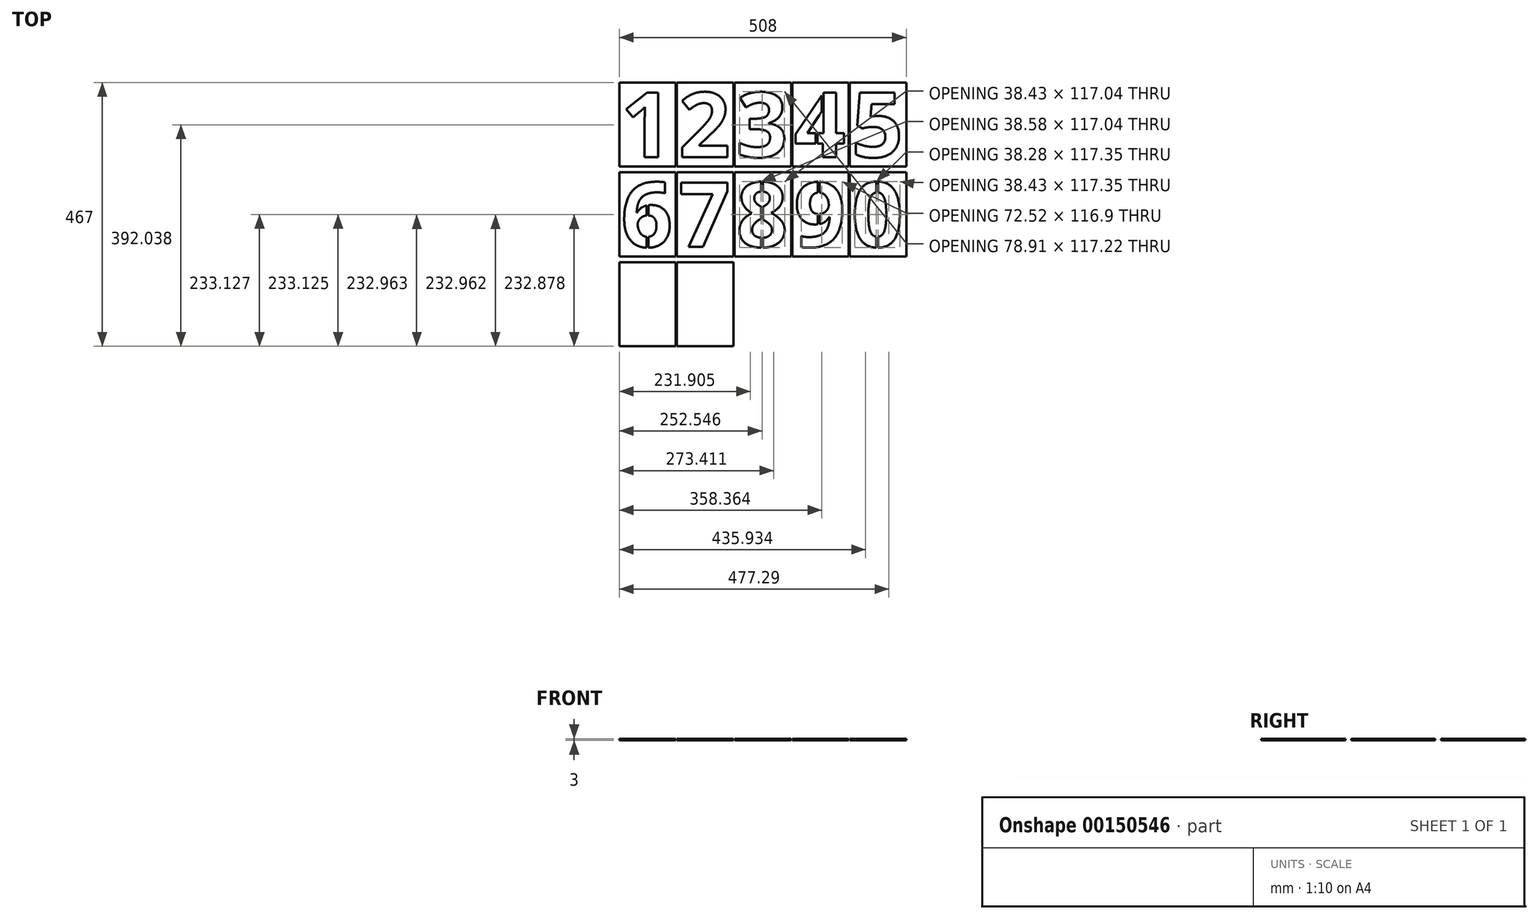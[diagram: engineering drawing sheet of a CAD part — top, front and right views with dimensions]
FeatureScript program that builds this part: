
annotation { "Feature Type Name" : "Feature", "Feature Type Description" : "" }
export const myFeature = defineFeature(function(context is Context, id is Id, definition is map)
    precondition{}
    {
        {
            var Q0;
            Q0=qCreatedBy(makeId("Top.planeOp"),FACE);
            var sketch = newSketch(context, id + "F0", { "sketchPlane" : qUnion([Q0])});
            skLineSegment(sketch, "E0.top", {"start": v(274, 333) * mm, "end": v(-274, 333) * mm, "construction": true});
            skLineSegment(sketch, "E0.left", {"start": v(274, -174) * mm, "end": v(274, 333) * mm, "construction": true});
            skLineSegment(sketch, "E0.right", {"start": v(-274, -174) * mm, "end": v(-274, 333) * mm, "construction": true});
            skPoint(sketch, "E0.middle", {"position": v(0, 0) * mm});
            skLineSegment(sketch, "E1", {"start": v(-254, 333) * mm, "end": v(-254, -174) * mm, "construction": true});
            skLineSegment(sketch, "E2.bottom", {"start": v(-254, 313) * mm, "end": v(274, 313) * mm, "construction": true});
            skLineSegment(sketch, "E2.top", {"start": v(-254, 164) * mm, "end": v(274, 164) * mm, "construction": true});
            skLineSegment(sketch, "E2.left", {"start": v(-254, 313) * mm, "end": v(-254, 164) * mm});
            skLineSegment(sketch, "E3", {"start": v(-154, 313) * mm, "end": v(-154, 164) * mm});
            skLineSegment(sketch, "E4", {"start": v(-254, 313) * mm, "end": v(-154, 313) * mm});
            skLineSegment(sketch, "E5", {"start": v(-254, 164) * mm, "end": v(-154, 164) * mm});
            skLineSegment(sketch, "E6.0", {"start": v(-152, 313) * mm, "end": v(-152, 164) * mm});
            skLineSegment(sketch, "E7", {"start": v(-52, 313) * mm, "end": v(-52, 164) * mm});
            skLineSegment(sketch, "E8.0", {"start": v(-50, 313) * mm, "end": v(-50, 164) * mm});
            skLineSegment(sketch, "E9", {"start": v(-152, 313) * mm, "end": v(-52, 313) * mm});
            skLineSegment(sketch, "E10", {"start": v(-152, 164) * mm, "end": v(-52, 164) * mm});
            skLineSegment(sketch, "E11", {"start": v(50, 313) * mm, "end": v(50, 164) * mm});
            skLineSegment(sketch, "E12.0", {"start": v(52, 313) * mm, "end": v(52, 164) * mm});
            skLineSegment(sketch, "E13", {"start": v(152, 313) * mm, "end": v(152, 164) * mm});
            skLineSegment(sketch, "E14.0", {"start": v(154, 313) * mm, "end": v(154, 164) * mm});
            skLineSegment(sketch, "E15", {"start": v(254, 313) * mm, "end": v(254, 164) * mm});
            skLineSegment(sketch, "E16", {"start": v(-50, 313) * mm, "end": v(50, 313) * mm});
            skLineSegment(sketch, "E17", {"start": v(52, 313) * mm, "end": v(152, 313) * mm});
            skLineSegment(sketch, "E18", {"start": v(154, 313) * mm, "end": v(254, 313) * mm});
            skLineSegment(sketch, "E19", {"start": v(254, 164) * mm, "end": v(154, 164) * mm});
            skLineSegment(sketch, "E20", {"start": v(152, 164) * mm, "end": v(52, 164) * mm});
            skLineSegment(sketch, "E21", {"start": v(50, 164) * mm, "end": v(-50, 164) * mm});
            skLineSegment(sketch, "E22.0", {"start": v(-261, 159) * mm, "end": v(267, 159) * mm, "construction": true});
            skLineSegment(sketch, "E23.MirrorCS", {"start": v(-52, 5) * mm, "end": v(-52, 154) * mm});
            skLineSegment(sketch, "E24.MirrorCS", {"start": v(254, 5) * mm, "end": v(254, 154) * mm});
            skLineSegment(sketch, "E25.MirrorCS", {"start": v(-254, 154) * mm, "end": v(-154, 154) * mm});
            skLineSegment(sketch, "E26.MirrorCS", {"start": v(-254, 5) * mm, "end": v(-154, 5) * mm});
            skLineSegment(sketch, "E27.MirrorCS", {"start": v(-152, 154) * mm, "end": v(-52, 154) * mm});
            skLineSegment(sketch, "E28.MirrorCS", {"start": v(154, 5) * mm, "end": v(254, 5) * mm});
            skLineSegment(sketch, "E29.MirrorCS", {"start": v(-152, 5) * mm, "end": v(-152, 154) * mm});
            skLineSegment(sketch, "E30.MirrorCS", {"start": v(154, 5) * mm, "end": v(154, 154) * mm});
            skLineSegment(sketch, "E31.MirrorCS", {"start": v(52, 5) * mm, "end": v(52, 154) * mm});
            skLineSegment(sketch, "E32.MirrorCS", {"start": v(-50, 5) * mm, "end": v(50, 5) * mm});
            skLineSegment(sketch, "E33.MirrorCS", {"start": v(-152, 5) * mm, "end": v(-52, 5) * mm});
            skLineSegment(sketch, "E34.MirrorCS", {"start": v(52, 5) * mm, "end": v(152, 5) * mm});
            skLineSegment(sketch, "E35.MirrorCS", {"start": v(50, 5) * mm, "end": v(50, 154) * mm});
            skLineSegment(sketch, "E36.MirrorCS", {"start": v(254, 154) * mm, "end": v(154, 154) * mm});
            skLineSegment(sketch, "E37.MirrorCS", {"start": v(-254, 5) * mm, "end": v(-254, 154) * mm});
            skLineSegment(sketch, "E38.MirrorCS", {"start": v(-154, 5) * mm, "end": v(-154, 154) * mm});
            skLineSegment(sketch, "E39.MirrorCS", {"start": v(50, 154) * mm, "end": v(-50, 154) * mm});
            skLineSegment(sketch, "E40.MirrorCS", {"start": v(152, 5) * mm, "end": v(152, 154) * mm});
            skLineSegment(sketch, "E41.MirrorCS", {"start": v(152, 154) * mm, "end": v(52, 154) * mm});
            skLineSegment(sketch, "E42.MirrorCS", {"start": v(-50, 5) * mm, "end": v(-50, 154) * mm});
            skLineSegment(sketch, "E43", {"start": v(-254, 0) * mm, "end": v(274, 0) * mm, "construction": true});
            skLineSegment(sketch, "E44.MirrorCS", {"start": v(-152, -5) * mm, "end": v(-152, -154) * mm});
            skLineSegment(sketch, "E45.MirrorCS", {"start": v(-152, -154) * mm, "end": v(-52, -154) * mm});
            skLineSegment(sketch, "E46.MirrorCS", {"start": v(-254, -5) * mm, "end": v(-154, -5) * mm});
            skLineSegment(sketch, "E47.MirrorCS", {"start": v(-254, -154) * mm, "end": v(-154, -154) * mm});
            skLineSegment(sketch, "E48.MirrorCS", {"start": v(-52, -5) * mm, "end": v(-52, -154) * mm});
            skLineSegment(sketch, "E49.MirrorCS", {"start": v(-152, -5) * mm, "end": v(-52, -5) * mm});
            skLineSegment(sketch, "E50.MirrorCS", {"start": v(-154, -5) * mm, "end": v(-154, -154) * mm});
            skLineSegment(sketch, "E51.MirrorCS", {"start": v(-254, -5) * mm, "end": v(-254, -154) * mm});
            skLineSegment(sketch, "E52", {"start": v(-254, 181) * mm, "end": v(254, 181) * mm, "construction": true});
            skLineSegment(sketch, "E53", {"start": v(-251, 313) * mm, "end": v(-251, 159) * mm, "construction": true});
            skText(sketch, "E54", { "text": "1", "fontName": "OpenSans-Bold.ttf"});
            skLineSegment(sketch, "E55", {"start": v(-149, 313) * mm, "end": v(-149, -154) * mm, "construction": true});
            skText(sketch, "E56", { "text": "2", "fontName": "OpenSans-Bold.ttf"});
            skLineSegment(sketch, "E57", {"start": v(-47, 313) * mm, "end": v(-47, 5) * mm, "construction": true});
            skText(sketch, "E58", { "text": "3", "fontName": "OpenSans-Bold.ttf"});
            skLineSegment(sketch, "E59", {"start": v(55, 313) * mm, "end": v(55, 5) * mm, "construction": true});
            skText(sketch, "E60", { "text": "4", "fontName": "OpenSans-Bold.ttf"});
            skLineSegment(sketch, "E61", {"start": v(157.03, 313) * mm, "end": v(157.03, 5) * mm, "construction": true});
            skText(sketch, "E62", { "text": "5", "fontName": "OpenSans-Bold.ttf"});
            skLineSegment(sketch, "E63", {"start": v(-254, 22) * mm, "end": v(254, 22) * mm, "construction": true});
            skLineSegment(sketch, "E64", {"start": v(-251, 159) * mm, "end": v(-251, 0) * mm, "construction": true});
            skText(sketch, "E65", { "text": "6", "fontName": "OpenSans-Bold.ttf"});
            skText(sketch, "E66", { "text": "7", "fontName": "OpenSans-Bold.ttf"});
            skText(sketch, "E67", { "text": "8\n", "fontName": "OpenSans-Bold.ttf"});
            skText(sketch, "E68", { "text": "9", "fontName": "OpenSans-Bold.ttf"});
            skText(sketch, "E69", { "text": "0", "fontName": "OpenSans-Bold.ttf"});
            skLineSegment(sketch, "E70", {"start": v(-274, -174) * mm, "end": v(274, -174) * mm, "construction": true});
            const initialGuessF0  = {"E54": [-0.251, 0.181, 1, 0, 0.115], "E56": [-0.149, 0.181, 1, 0, 0.115], "E58": [-0.047, 0.181, 1, 0, 0.115], "E60": [0.055, 0.181, 1, 0, 0.115], "E62": [0.15703, 0.181, 1, 0, 0.115], "E65": [-0.251, 0.022, 1, 0, 0.115], "E66": [-0.149, 0.022, 1, 0, 0.115], "E67": [-0.047, 0.022, 1, 0, 0.115], "E68": [0.055, 0.022, 1, 0, 0.115], "E69": [0.15703, 0.022, 1, 0, 0.115]};
            skSetInitialGuess(sketch, initialGuessF0);
            skSolve(sketch);
        }
        {
            var Q0;
            Q0=makeQuery(id+"F0.imprint","IMPRINT",FACE,{"disambiguationData":[TD([[makeQuery(id+"F0.imprint","IMPRINT",EDGE,{"derivedFrom":sQuery(id+"F0.wireOp",EDGE,"E2.left")}),1.0]])]});
            var Q1;
            Q1=makeQuery(id+"F0.imprint","IMPRINT",FACE,{"disambiguationData":[TD([[makeQuery(id+"F0.imprint","IMPRINT",EDGE,{"derivedFrom":sQuery(id+"F0.wireOp",EDGE,"E6.0")}),1.0]])]});
            var Q2;
            Q2=makeQuery(id+"F0.imprint","IMPRINT",FACE,{"disambiguationData":[TD([[makeQuery(id+"F0.imprint","IMPRINT",EDGE,{"derivedFrom":sQuery(id+"F0.wireOp",EDGE,"E8.0")}),1.0]])]});
            var Q3;
            Q3=makeQuery(id+"F0.imprint","IMPRINT",FACE,{"disambiguationData":[TD([[makeQuery(id+"F0.imprint","IMPRINT",EDGE,{"derivedFrom":sQuery(id+"F0.wireOp",EDGE,"E12.0")}),1.0]])]});
            var Q4;
            Q4=makeQuery(id+"F0.imprint","IMPRINT",FACE,{"disambiguationData":[TD([[makeQuery(id+"F0.imprint","IMPRINT",EDGE,{"derivedFrom":sQuery(id+"F0.wireOp",EDGE,"E60.sketch_text.stroke-11")}),1.0]])]});
            var Q5;
            Q5=makeQuery(id+"F0.imprint","IMPRINT",FACE,{"disambiguationData":[TD([[makeQuery(id+"F0.imprint","IMPRINT",EDGE,{"derivedFrom":sQuery(id+"F0.wireOp",EDGE,"E14.0")}),1.0]])]});
            var Q6;
            Q6=makeQuery(id+"F0.imprint","IMPRINT",FACE,{"disambiguationData":[TD([[makeQuery(id+"F0.imprint","IMPRINT",EDGE,{"derivedFrom":sQuery(id+"F0.wireOp",EDGE,"E25.MirrorCS")}),-1.0]])]});
            var Q7;
            Q7=makeQuery(id+"F0.imprint","IMPRINT",FACE,{"disambiguationData":[TD([[makeQuery(id+"F0.imprint","IMPRINT",EDGE,{"derivedFrom":sQuery(id+"F0.wireOp",EDGE,"E65.sketch_text.stroke-17")}),1.0]])]});
            var Q8;
            Q8=makeQuery(id+"F0.imprint","IMPRINT",FACE,{"disambiguationData":[TD([[makeQuery(id+"F0.imprint","IMPRINT",EDGE,{"derivedFrom":sQuery(id+"F0.wireOp",EDGE,"E23.MirrorCS")}),1.0]])]});
            var Q9;
            Q9=makeQuery(id+"F0.imprint","IMPRINT",FACE,{"disambiguationData":[TD([[makeQuery(id+"F0.imprint","IMPRINT",EDGE,{"derivedFrom":sQuery(id+"F0.wireOp",EDGE,"E32.MirrorCS")}),1.0]])]});
            var Q10;
            Q10=makeQuery(id+"F0.imprint","IMPRINT",FACE,{"disambiguationData":[TD([[makeQuery(id+"F0.imprint","IMPRINT",EDGE,{"derivedFrom":sQuery(id+"F0.wireOp",EDGE,"E67.sketch_text.stroke-23")}),1.0]])]});
            var Q11;
            Q11=makeQuery(id+"F0.imprint","IMPRINT",FACE,{"disambiguationData":[TD([[makeQuery(id+"F0.imprint","IMPRINT",EDGE,{"derivedFrom":sQuery(id+"F0.wireOp",EDGE,"E67.sketch_text.stroke-16")}),1.0]])]});
            var Q12;
            Q12=makeQuery(id+"F0.imprint","IMPRINT",FACE,{"disambiguationData":[TD([[makeQuery(id+"F0.imprint","IMPRINT",EDGE,{"derivedFrom":sQuery(id+"F0.wireOp",EDGE,"E68.sketch_text.stroke-18")}),1.0]])]});
            var Q13;
            Q13=makeQuery(id+"F0.imprint","IMPRINT",FACE,{"disambiguationData":[TD([[makeQuery(id+"F0.imprint","IMPRINT",EDGE,{"derivedFrom":sQuery(id+"F0.wireOp",EDGE,"E31.MirrorCS")}),-1.0]])]});
            var Q14;
            Q14=makeQuery(id+"F0.imprint","IMPRINT",FACE,{"disambiguationData":[TD([[makeQuery(id+"F0.imprint","IMPRINT",EDGE,{"derivedFrom":sQuery(id+"F0.wireOp",EDGE,"E69.sketch_text.stroke-8")}),1.0]])]});
            var Q15;
            Q15=makeQuery(id+"F0.imprint","IMPRINT",FACE,{"disambiguationData":[TD([[makeQuery(id+"F0.imprint","IMPRINT",EDGE,{"derivedFrom":sQuery(id+"F0.wireOp",EDGE,"E24.MirrorCS")}),1.0]])]});
            var Q16;
            Q16=makeQuery(id+"F0.imprint","IMPRINT",FACE,{"disambiguationData":[TD([[makeQuery(id+"F0.imprint","IMPRINT",EDGE,{"derivedFrom":sQuery(id+"F0.wireOp",EDGE,"E46.MirrorCS")}),-1.0]])]});
            var Q17;
            Q17=makeQuery(id+"F0.imprint","IMPRINT",FACE,{"disambiguationData":[TD([[makeQuery(id+"F0.imprint","IMPRINT",EDGE,{"derivedFrom":sQuery(id+"F0.wireOp",EDGE,"E44.MirrorCS")}),1.0]])]});
            extrude(context, id + "F1", {"entities" : qUnion([Q0, Q1, Q2, Q3, Q4, Q5, Q6, Q7, Q8, Q9, Q10, Q11, Q12, Q13, Q14, Q15, Q16, Q17]), "depth" : 3 * mm});
        }
        {
            var Q0;
            Q0=makeQuery(id+"F1.opExtrude","CAP_FACE",FACE,{"disambiguationData":[OSD([sQuery(id+"F0.wireOp",EDGE,"E12.0"),sQuery(id+"F0.wireOp",EDGE,"E13"),sQuery(id+"F0.wireOp",EDGE,"E17"),sQuery(id+"F0.wireOp",EDGE,"E20"),sQuery(id+"F0.wireOp",EDGE,"E60.sketch_text.stroke-0"),sQuery(id+"F0.wireOp",EDGE,"E60.sketch_text.stroke-1"),sQuery(id+"F0.wireOp",EDGE,"E60.sketch_text.stroke-2"),sQuery(id+"F0.wireOp",EDGE,"E60.sketch_text.stroke-3"),sQuery(id+"F0.wireOp",EDGE,"E60.sketch_text.stroke-4"),sQuery(id+"F0.wireOp",EDGE,"E60.sketch_text.stroke-5"),sQuery(id+"F0.wireOp",EDGE,"E60.sketch_text.stroke-6"),sQuery(id+"F0.wireOp",EDGE,"E60.sketch_text.stroke-7"),sQuery(id+"F0.wireOp",EDGE,"E60.sketch_text.stroke-8"),sQuery(id+"F0.wireOp",EDGE,"E60.sketch_text.stroke-9"),sQuery(id+"F0.wireOp",EDGE,"E60.sketch_text.stroke-10")])],"isStart":false});
            var sketch = newSketch(context, id + "F2", { "sketchPlane" : qUnion([Q0])});
            skLineSegment(sketch, "E71.bottom", {"start": v(93.39, 204.63) * mm, "end": v(96.39, 204.63) * mm});
            skLineSegment(sketch, "E71.top", {"start": v(93.39, 223.35) * mm, "end": v(96.39, 223.35) * mm});
            skLineSegment(sketch, "E71.left", {"start": v(93.39, 204.63) * mm, "end": v(93.39, 223.35) * mm});
            skLineSegment(sketch, "E71.right", {"start": v(96.39, 204.63) * mm, "end": v(96.39, 223.35) * mm});
            skLineSegment(sketch, "E72.bottom", {"start": v(107.4, 295.03) * mm, "end": v(104.4, 295.03) * mm});
            skLineSegment(sketch, "E72.left", {"start": v(107.4, 295.03) * mm, "end": v(107.4, 267.42) * mm});
            skLineSegment(sketch, "E72.right", {"start": v(104.4, 295.03) * mm, "end": v(104.4, 223.35) * mm});
            skLineSegment(sketch, "E73", {"start": v(107.4, 267.42) * mm, "end": v(107.4, 223.35) * mm});
            skLineSegment(sketch, "E74", {"start": v(107.4, 223.35) * mm, "end": v(106.39, 223.35) * mm});
            skLineSegment(sketch, "E75", {"start": v(106.39, 223.35) * mm, "end": v(104.4, 223.35) * mm});
            skPoint(sketch, "E72.top.end.orphan", {"position": v(104.4, 267.42) * mm});
            skSolve(sketch);
        }
        {
            var Q0;
            {var subQ0=sQuery(id+"F2.wireOp",EDGE,"E73");Q0=makeQuery(id+"F2.imprint","IMPRINT",FACE,{"disambiguationData":[TD([[makeQuery(id+"F2.imprint","IMPRINT",EDGE,{"derivedFrom":subQ0}),-1.0]])]});}
            var Q1;
            Q1=makeQuery(id+"F2.imprint","IMPRINT",FACE,{"disambiguationData":[TD([[makeQuery(id+"F2.imprint","IMPRINT",EDGE,{"derivedFrom":sQuery(id+"F2.wireOp",EDGE,"E71.bottom")}),-1.0]])]});
            var Q2;
            Q2=makeQuery(id+"F1.opExtrude","CAP_FACE",FACE,{"disambiguationData":[OSD([sQuery(id+"F0.wireOp",EDGE,"E60.sketch_text.stroke-11"),sQuery(id+"F0.wireOp",EDGE,"E60.sketch_text.stroke-12"),sQuery(id+"F0.wireOp",EDGE,"E60.sketch_text.stroke-13"),sQuery(id+"F0.wireOp",EDGE,"E60.sketch_text.stroke-14"),sQuery(id+"F0.wireOp",EDGE,"E60.sketch_text.stroke-15"),sQuery(id+"F0.wireOp",EDGE,"E60.sketch_text.stroke-16"),sQuery(id+"F0.wireOp",EDGE,"E60.sketch_text.stroke-17")])],"isStart":true});
            extrude(context, id + "F3", {"entities" : qUnion([Q0, Q1]), "operationType" : NewBodyOperationType.ADD, "endBound" : BoundingType.UP_TO_SURFACE, "oppositeDirection" : true, "endBoundEntityFace" : qUnion([Q2]), "depth" : 25 * mm});
        }
        {
            var Q0;
            Q0=makeQuery(id+"F1.opExtrude","CAP_FACE",FACE,{"disambiguationData":[OSD([sQuery(id+"F0.wireOp",EDGE,"E65.sketch_text.stroke-17"),sQuery(id+"F0.wireOp",EDGE,"E65.sketch_text.stroke-18"),sQuery(id+"F0.wireOp",EDGE,"E65.sketch_text.stroke-19"),sQuery(id+"F0.wireOp",EDGE,"E65.sketch_text.stroke-20"),sQuery(id+"F0.wireOp",EDGE,"E65.sketch_text.stroke-21"),sQuery(id+"F0.wireOp",EDGE,"E65.sketch_text.stroke-22"),sQuery(id+"F0.wireOp",EDGE,"E65.sketch_text.stroke-23"),sQuery(id+"F0.wireOp",EDGE,"E65.sketch_text.stroke-24")])],"isStart":false});
            var sketch = newSketch(context, id + "F4", { "sketchPlane" : qUnion([Q0])});
            skLineSegment(sketch, "E76", {"start": v(-203.73, 98.87) * mm, "end": v(-204.2, 20.1) * mm, "construction": true});
            skLineSegment(sketch, "E77.bottom", {"start": v(-205.7, 98.87) * mm, "end": v(-202.7, 98.87) * mm});
            skLineSegment(sketch, "E77.top", {"start": v(-205.7, 20.1) * mm, "end": v(-202.7, 20.1) * mm});
            skLineSegment(sketch, "E77.left", {"start": v(-205.7, 98.87) * mm, "end": v(-205.7, 20.1) * mm});
            skLineSegment(sketch, "E77.right", {"start": v(-202.7, 98.87) * mm, "end": v(-202.7, 20.1) * mm});
            skSolve(sketch);
        }
        {
            var Q0;
            Q0 = qSketchRegion(id + "F4", true);
            var Q1;
            Q1=makeQuery(id+"F1.opExtrude","CAP_FACE",FACE,{"disambiguationData":[OSD([sQuery(id+"F0.wireOp",EDGE,"E65.sketch_text.stroke-17"),sQuery(id+"F0.wireOp",EDGE,"E65.sketch_text.stroke-18"),sQuery(id+"F0.wireOp",EDGE,"E65.sketch_text.stroke-19"),sQuery(id+"F0.wireOp",EDGE,"E65.sketch_text.stroke-20"),sQuery(id+"F0.wireOp",EDGE,"E65.sketch_text.stroke-21"),sQuery(id+"F0.wireOp",EDGE,"E65.sketch_text.stroke-22"),sQuery(id+"F0.wireOp",EDGE,"E65.sketch_text.stroke-23"),sQuery(id+"F0.wireOp",EDGE,"E65.sketch_text.stroke-24")])],"isStart":true});
            extrude(context, id + "F5", {"entities" : qUnion([Q0]), "operationType" : NewBodyOperationType.ADD, "endBound" : BoundingType.UP_TO_SURFACE, "oppositeDirection" : true, "endBoundEntityFace" : qUnion([Q1]), "depth" : 25 * mm});
        }
        {
            var Q0;
            Q0=makeQuery(id+"F1.opExtrude","CAP_FACE",FACE,{"disambiguationData":[OSD([sQuery(id+"F0.wireOp",EDGE,"E32.MirrorCS"),sQuery(id+"F0.wireOp",EDGE,"E35.MirrorCS"),sQuery(id+"F0.wireOp",EDGE,"E39.MirrorCS"),sQuery(id+"F0.wireOp",EDGE,"E42.MirrorCS"),sQuery(id+"F0.wireOp",EDGE,"E67.sketch_text.stroke-0"),sQuery(id+"F0.wireOp",EDGE,"E67.sketch_text.stroke-1"),sQuery(id+"F0.wireOp",EDGE,"E67.sketch_text.stroke-2"),sQuery(id+"F0.wireOp",EDGE,"E67.sketch_text.stroke-3"),sQuery(id+"F0.wireOp",EDGE,"E67.sketch_text.stroke-4"),sQuery(id+"F0.wireOp",EDGE,"E67.sketch_text.stroke-5"),sQuery(id+"F0.wireOp",EDGE,"E67.sketch_text.stroke-6"),sQuery(id+"F0.wireOp",EDGE,"E67.sketch_text.stroke-7"),sQuery(id+"F0.wireOp",EDGE,"E67.sketch_text.stroke-8"),sQuery(id+"F0.wireOp",EDGE,"E67.sketch_text.stroke-9"),sQuery(id+"F0.wireOp",EDGE,"E67.sketch_text.stroke-10"),sQuery(id+"F0.wireOp",EDGE,"E67.sketch_text.stroke-11"),sQuery(id+"F0.wireOp",EDGE,"E67.sketch_text.stroke-12"),sQuery(id+"F0.wireOp",EDGE,"E67.sketch_text.stroke-13"),sQuery(id+"F0.wireOp",EDGE,"E67.sketch_text.stroke-14"),sQuery(id+"F0.wireOp",EDGE,"E67.sketch_text.stroke-15")])],"isStart":false});
            var sketch = newSketch(context, id + "F6", { "sketchPlane" : qUnion([Q0])});
            skLineSegment(sketch, "E78", {"start": v(-1.3, 144.27) * mm, "end": v(-1.3, 20.43) * mm, "construction": true});
            skLineSegment(sketch, "E79.bottom", {"start": v(-2.8, 144.27) * mm, "end": v(0.2, 144.27) * mm});
            skLineSegment(sketch, "E79.top", {"start": v(-2.8, 15.09) * mm, "end": v(0.2, 15.09) * mm});
            skLineSegment(sketch, "E79.left", {"start": v(-2.8, 144.27) * mm, "end": v(-2.8, 15.09) * mm});
            skLineSegment(sketch, "E79.right", {"start": v(0.2, 144.27) * mm, "end": v(0.2, 15.09) * mm});
            skSolve(sketch);
        }
        {
            var Q0;
            Q0 = qSketchRegion(id + "F6", true);
            var Q1;
            Q1=makeQuery(id+"F1.opExtrude","CAP_FACE",FACE,{"disambiguationData":[OSD([sQuery(id+"F0.wireOp",EDGE,"E67.sketch_text.stroke-16"),sQuery(id+"F0.wireOp",EDGE,"E67.sketch_text.stroke-17"),sQuery(id+"F0.wireOp",EDGE,"E67.sketch_text.stroke-18"),sQuery(id+"F0.wireOp",EDGE,"E67.sketch_text.stroke-19"),sQuery(id+"F0.wireOp",EDGE,"E67.sketch_text.stroke-20"),sQuery(id+"F0.wireOp",EDGE,"E67.sketch_text.stroke-21"),sQuery(id+"F0.wireOp",EDGE,"E67.sketch_text.stroke-22")])],"isStart":true});
            extrude(context, id + "F7", {"entities" : qUnion([Q0]), "operationType" : NewBodyOperationType.ADD, "endBound" : BoundingType.UP_TO_SURFACE, "oppositeDirection" : true, "endBoundEntityFace" : qUnion([Q1]), "depth" : 25 * mm});
        }
        {
            var Q0;
            Q0=makeQuery(id+"F1.opExtrude","CAP_FACE",FACE,{"disambiguationData":[OSD([sQuery(id+"F0.wireOp",EDGE,"E31.MirrorCS"),sQuery(id+"F0.wireOp",EDGE,"E34.MirrorCS"),sQuery(id+"F0.wireOp",EDGE,"E40.MirrorCS"),sQuery(id+"F0.wireOp",EDGE,"E41.MirrorCS"),sQuery(id+"F0.wireOp",EDGE,"E68.sketch_text.stroke-0"),sQuery(id+"F0.wireOp",EDGE,"E68.sketch_text.stroke-1"),sQuery(id+"F0.wireOp",EDGE,"E68.sketch_text.stroke-2"),sQuery(id+"F0.wireOp",EDGE,"E68.sketch_text.stroke-3"),sQuery(id+"F0.wireOp",EDGE,"E68.sketch_text.stroke-4"),sQuery(id+"F0.wireOp",EDGE,"E68.sketch_text.stroke-5"),sQuery(id+"F0.wireOp",EDGE,"E68.sketch_text.stroke-6"),sQuery(id+"F0.wireOp",EDGE,"E68.sketch_text.stroke-7"),sQuery(id+"F0.wireOp",EDGE,"E68.sketch_text.stroke-8"),sQuery(id+"F0.wireOp",EDGE,"E68.sketch_text.stroke-9"),sQuery(id+"F0.wireOp",EDGE,"E68.sketch_text.stroke-10"),sQuery(id+"F0.wireOp",EDGE,"E68.sketch_text.stroke-11"),sQuery(id+"F0.wireOp",EDGE,"E68.sketch_text.stroke-12"),sQuery(id+"F0.wireOp",EDGE,"E68.sketch_text.stroke-13"),sQuery(id+"F0.wireOp",EDGE,"E68.sketch_text.stroke-14"),sQuery(id+"F0.wireOp",EDGE,"E68.sketch_text.stroke-15"),sQuery(id+"F0.wireOp",EDGE,"E68.sketch_text.stroke-16"),sQuery(id+"F0.wireOp",EDGE,"E68.sketch_text.stroke-17")])],"isStart":false});
            var sketch = newSketch(context, id + "F8", { "sketchPlane" : qUnion([Q0])});
            skLineSegment(sketch, "E80", {"start": v(98.9, 141.64) * mm, "end": v(98.9, 62.11) * mm, "construction": true});
            skLineSegment(sketch, "E81.bottom", {"start": v(97.4, 141.64) * mm, "end": v(100.4, 141.64) * mm});
            skLineSegment(sketch, "E81.top", {"start": v(97.4, 58.38) * mm, "end": v(100.4, 58.38) * mm});
            skLineSegment(sketch, "E81.left", {"start": v(97.4, 141.64) * mm, "end": v(97.4, 58.38) * mm});
            skLineSegment(sketch, "E81.right", {"start": v(100.4, 141.64) * mm, "end": v(100.4, 58.38) * mm});
            skSolve(sketch);
        }
        {
            var Q0;
            {var subQ1=makeQuery(id+"F1.opExtrude","CAP_EDGE",EDGE,{"disambiguationData":[OSD([sQuery(id+"F0.wireOp",EDGE,"E68.sketch_text.stroke-14")])],"isStart":false});var subQ3=sQuery(id+"F8.wireOp",EDGE,"E81.left");var subQ4=makeQuery(id+"F8.imprint","INTERSECT",VERTEX,{"derivedFrom":[subQ1,subQ3]});Q0=makeQuery(id+"F8.imprint","IMPRINT",FACE,{"disambiguationData":[TD([[makeQuery(id+"F8.imprint","IMPRINT",EDGE,{"disambiguationData":[TD([[subQ4,-1.0]])],"derivedFrom":subQ3}),1.0]])]});}
            var Q1;
            Q1=makeQuery(id+"F1.opExtrude","CAP_FACE",FACE,{"disambiguationData":[OSD([sQuery(id+"F0.wireOp",EDGE,"E68.sketch_text.stroke-18"),sQuery(id+"F0.wireOp",EDGE,"E68.sketch_text.stroke-19"),sQuery(id+"F0.wireOp",EDGE,"E68.sketch_text.stroke-20"),sQuery(id+"F0.wireOp",EDGE,"E68.sketch_text.stroke-21"),sQuery(id+"F0.wireOp",EDGE,"E68.sketch_text.stroke-22"),sQuery(id+"F0.wireOp",EDGE,"E68.sketch_text.stroke-23"),sQuery(id+"F0.wireOp",EDGE,"E68.sketch_text.stroke-24"),sQuery(id+"F0.wireOp",EDGE,"E68.sketch_text.stroke-25")])],"isStart":true});
            extrude(context, id + "F9", {"entities" : qUnion([Q0]), "operationType" : NewBodyOperationType.ADD, "endBound" : BoundingType.UP_TO_SURFACE, "oppositeDirection" : true, "endBoundEntityFace" : qUnion([Q1]), "depth" : 25 * mm});
        }
        {
            var Q0;
            Q0=makeQuery(id+"F1.opExtrude","CAP_FACE",FACE,{"disambiguationData":[OSD([sQuery(id+"F0.wireOp",EDGE,"E24.MirrorCS"),sQuery(id+"F0.wireOp",EDGE,"E28.MirrorCS"),sQuery(id+"F0.wireOp",EDGE,"E30.MirrorCS"),sQuery(id+"F0.wireOp",EDGE,"E36.MirrorCS"),sQuery(id+"F0.wireOp",EDGE,"E69.sketch_text.stroke-0"),sQuery(id+"F0.wireOp",EDGE,"E69.sketch_text.stroke-1"),sQuery(id+"F0.wireOp",EDGE,"E69.sketch_text.stroke-2"),sQuery(id+"F0.wireOp",EDGE,"E69.sketch_text.stroke-3"),sQuery(id+"F0.wireOp",EDGE,"E69.sketch_text.stroke-4"),sQuery(id+"F0.wireOp",EDGE,"E69.sketch_text.stroke-5"),sQuery(id+"F0.wireOp",EDGE,"E69.sketch_text.stroke-6"),sQuery(id+"F0.wireOp",EDGE,"E69.sketch_text.stroke-7")])],"isStart":false});
            var sketch = newSketch(context, id + "F10", { "sketchPlane" : qUnion([Q0])});
            skLineSegment(sketch, "E82", {"start": v(202.57, 145) * mm, "end": v(202.57, 20.43) * mm, "construction": true});
            skLineSegment(sketch, "E83.bottom", {"start": v(201.07, 145) * mm, "end": v(204.07, 145) * mm});
            skLineSegment(sketch, "E83.top", {"start": v(201.07, 16.9) * mm, "end": v(204.07, 16.9) * mm});
            skLineSegment(sketch, "E83.left", {"start": v(201.07, 145) * mm, "end": v(201.07, 16.9) * mm});
            skLineSegment(sketch, "E83.right", {"start": v(204.07, 145) * mm, "end": v(204.07, 16.9) * mm});
            skSolve(sketch);
        }
        {
            var Q0;
            Q0 = qSketchRegion(id + "F10", true);
            var Q1;
            Q1=makeQuery(id+"F1.opExtrude","CAP_FACE",FACE,{"disambiguationData":[OSD([sQuery(id+"F0.wireOp",EDGE,"E69.sketch_text.stroke-8"),sQuery(id+"F0.wireOp",EDGE,"E69.sketch_text.stroke-9"),sQuery(id+"F0.wireOp",EDGE,"E69.sketch_text.stroke-10"),sQuery(id+"F0.wireOp",EDGE,"E69.sketch_text.stroke-11"),sQuery(id+"F0.wireOp",EDGE,"E69.sketch_text.stroke-12"),sQuery(id+"F0.wireOp",EDGE,"E69.sketch_text.stroke-13"),sQuery(id+"F0.wireOp",EDGE,"E69.sketch_text.stroke-14"),sQuery(id+"F0.wireOp",EDGE,"E69.sketch_text.stroke-15")])],"isStart":true});
            extrude(context, id + "F11", {"entities" : qUnion([Q0]), "operationType" : NewBodyOperationType.ADD, "endBound" : BoundingType.UP_TO_SURFACE, "oppositeDirection" : true, "endBoundEntityFace" : qUnion([Q1]), "depth" : 25 * mm});
        }
    });
